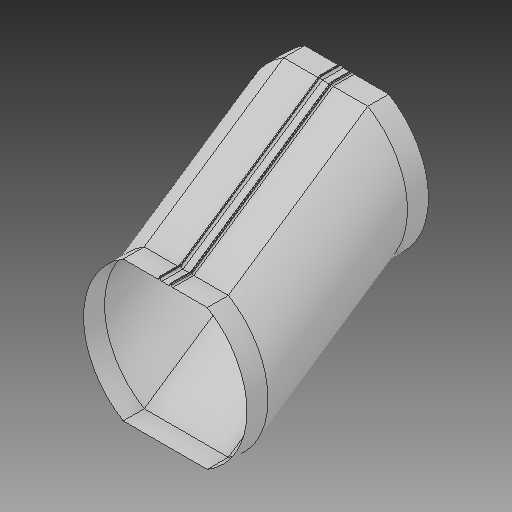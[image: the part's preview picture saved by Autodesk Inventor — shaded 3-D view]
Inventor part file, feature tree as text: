
AUTODESK INVENTOR PART (.ipt)
format: ipt  version: 2017 (Build 210142000, 142)  size: 217,088 bytes
history: native  units: in
note: dims shown in document units (in); Inventor stores cm internally (conversion verified against a paired STEP export)
features: sketch x2, extrude x2, plane x1, sweep x1, delete_face x1
ambient origin geometry x8: Origin, YZ Plane, XZ Plane, XY Plane, X Axis, Y Axis, Z Axis, Center Point
bodies: Solid1 (feature_tree)
feature tree (7):
  sketch  "Sketch1"  dims[d0=6.6667in d3=1.0in d4=0.0in d12=8.0in]
  extrude  "connection top"  Depth=8.0in
  plane  "Work Plane2"
  sweep  "ramp"
  extrude  "connection bottom"  Depth=0.0884in TaperAngle=0.0deg
  delete_face  "Delete Face1"
  sketch  "Sketch6"  dims[d28=8.0in d45=0.0in d46=0.0in d49=1.0in d50=0.0in d70=0.8521in d87=4.0in d88=0.5833in d89=3.8873in d90=3.8873in d91=1.7083in d92=0.0625in d93=0.0625in d94=1.6458in d95=0.25in d96=0.125in d98=0.0884in d99=45.0deg d100=3.3333in d101=0.125in d102=4.0in d103=0.5833in d104=3.8873in d105=3.8873in d106=1.7083in d107=0.0625in d108=0.0625in d109=1.6458in d110=0.25in d111=0.125in d113=0.0884in d114=45.0deg d115=3.3333in d116=0.125in]
